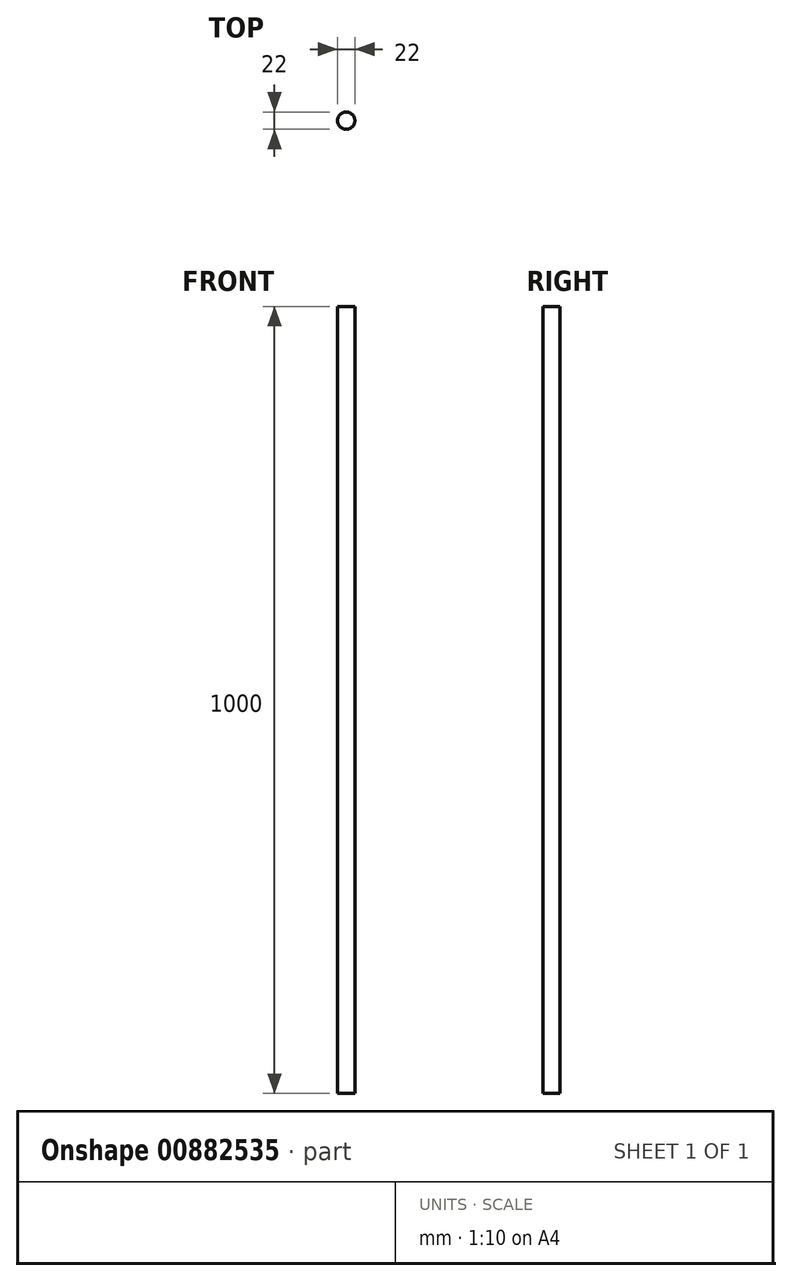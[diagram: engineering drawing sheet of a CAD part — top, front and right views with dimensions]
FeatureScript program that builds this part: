
annotation { "Feature Type Name" : "Feature", "Feature Type Description" : "" }
export const myFeature = defineFeature(function(context is Context, id is Id, definition is map)
    precondition{}
    {
        {
            var Q0;
            Q0=qCreatedBy(makeId("Top.planeOp"),FACE);
            var sketch = newSketch(context, id + "F0", { "sketchPlane" : qUnion([Q0])});
            skCircle(sketch, "E0", {"center": v(0, 0) * mm, "radius": 11 * mm});
            skSolve(sketch);
        }
        {
            var Q0;
            Q0 = qSketchRegion(id + "F0", true);
            extrude(context, id + "F1", {"entities" : qUnion([Q0]), "depth" : 1000 * mm, "offsetDistance" : 25 * mm});
        }
    });
